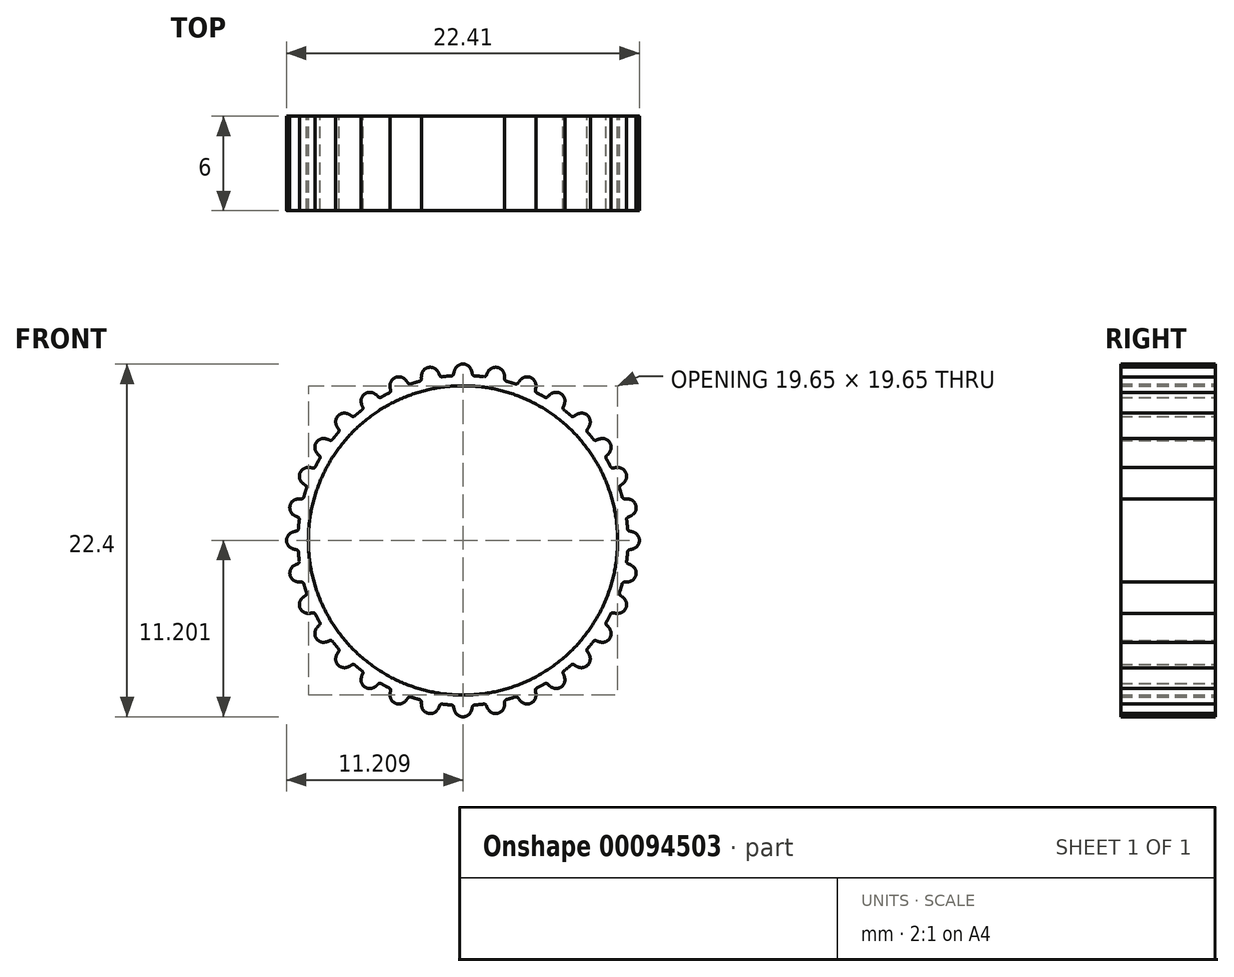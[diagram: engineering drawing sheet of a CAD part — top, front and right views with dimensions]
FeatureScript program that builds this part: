
annotation { "Feature Type Name" : "Feature", "Feature Type Description" : "" }
export const myFeature = defineFeature(function(context is Context, id is Id, definition is map)
    precondition{}
    {
        {
            var Q0;
            Q0=qCreatedBy(makeId("Front.planeOp"),FACE);
            var sketch = newSketch(context, id + "F0", { "sketchPlane" : qUnion([Q0])});
            skLineSegment(sketch, "E0", {"start": v(2.95, 2.18) * mm, "end": v(2.95, 0.8) * mm, "construction": true});
            skArc(sketch, "E1", {"start": v(2.95, 2.18) * mm, "mid": v(3.24, 2.1) * mm, "end": v(3.45, 1.87) * mm});
            skArc(sketch, "E2", {"start": v(3.45, 1.87) * mm, "mid": v(3.5, 1.72) * mm, "end": v(3.54, 1.56) * mm});
            skArc(sketch, "E3", {"start": v(3.54, 1.56) * mm, "mid": v(3.59, 1.48) * mm, "end": v(3.68, 1.43) * mm});
            skPoint(sketch, "E4", {"position": v(2.95, 0.8) * mm});
            skPoint(sketch, "E5", {"position": v(2.95, 1.43) * mm});
            skPoint(sketch, "E6", {"position": v(2.95, 1.18) * mm});
            skArc(sketch, "E7", {"start": v(2.95, 1.18) * mm, "mid": v(3.45, 1.17) * mm, "end": v(3.95, 1.13) * mm, "construction": true});
            skLineSegment(sketch, "E8", {"start": v(3.91, 0.76) * mm, "end": v(3.98, 1.4) * mm});
            skArc(sketch, "E9", {"start": v(3.68, 1.43) * mm, "mid": v(3.83, 1.42) * mm, "end": v(3.98, 1.4) * mm});
            skArc(sketch, "E10", {"start": v(2.95, 0.8) * mm, "mid": v(3.43, 0.8) * mm, "end": v(3.91, 0.76) * mm});
            skArc(sketch, "E11.MirrorCS", {"start": v(2.95, 2.18) * mm, "mid": v(2.65, 2.1) * mm, "end": v(2.45, 1.87) * mm});
            skArc(sketch, "E12.MirrorCS", {"start": v(2.45, 1.87) * mm, "mid": v(2.4, 1.72) * mm, "end": v(2.36, 1.56) * mm});
            skArc(sketch, "E13.MirrorCS", {"start": v(2.36, 1.56) * mm, "mid": v(2.31, 1.48) * mm, "end": v(2.22, 1.43) * mm});
            skArc(sketch, "E14.MirrorCS", {"start": v(2.22, 1.43) * mm, "mid": v(2.07, 1.42) * mm, "end": v(1.92, 1.4) * mm});
            skLineSegment(sketch, "E15.MirrorCS", {"start": v(1.99, 0.76) * mm, "end": v(1.92, 1.4) * mm});
            skArc(sketch, "E16.MirrorCS", {"start": v(2.95, 0.8) * mm, "mid": v(2.47, 0.8) * mm, "end": v(1.99, 0.76) * mm});
            skArc(sketch, "E17.1.0", {"start": v(0.33, 1.57) * mm, "mid": v(0.3, 1.4) * mm, "end": v(0.3, 1.25) * mm});
            skArc(sketch, "E17.1.1", {"start": v(0.76, 1.97) * mm, "mid": v(0.5, 1.83) * mm, "end": v(0.33, 1.57) * mm});
            skArc(sketch, "E17.1.2", {"start": v(1.03, 0.62) * mm, "mid": v(1.5, 0.7) * mm, "end": v(1.99, 0.76) * mm});
            skPoint(sketch, "E17.1.3", {"position": v(0.9, 1.23) * mm});
            skArc(sketch, "E17.1.4", {"start": v(1.31, 1.76) * mm, "mid": v(1.4, 1.62) * mm, "end": v(1.46, 1.48) * mm});
            skLineSegment(sketch, "E17.1.5", {"start": v(0.1, 0.38) * mm, "end": v(-0.1, 1) * mm});
            skArc(sketch, "E17.1.6", {"start": v(1.63, 1.38) * mm, "mid": v(1.77, 1.4) * mm, "end": v(1.92, 1.4) * mm});
            skArc(sketch, "E17.1.8", {"start": v(0.76, 1.97) * mm, "mid": v(1.07, 1.94) * mm, "end": v(1.31, 1.76) * mm});
            skPoint(sketch, "E17.1.9", {"position": v(1.03, 0.62) * mm});
            skArc(sketch, "E17.1.10", {"start": v(0.96, 0.98) * mm, "mid": v(1.45, 1.07) * mm, "end": v(1.95, 1.13) * mm, "construction": true});
            skArc(sketch, "E17.1.11", {"start": v(1.03, 0.62) * mm, "mid": v(0.56, 0.51) * mm, "end": v(0.1, 0.38) * mm});
            skPoint(sketch, "E17.1.12", {"position": v(0.96, 0.98) * mm});
            skArc(sketch, "E17.1.13", {"start": v(0.2, 1.1) * mm, "mid": v(0.05, 1.05) * mm, "end": v(-0.1, 1) * mm});
            skArc(sketch, "E17.1.14", {"start": v(1.46, 1.48) * mm, "mid": v(1.53, 1.4) * mm, "end": v(1.63, 1.38) * mm});
            skArc(sketch, "E17.1.15", {"start": v(0.3, 1.25) * mm, "mid": v(0.28, 1.15) * mm, "end": v(0.2, 1.1) * mm});
            skArc(sketch, "E17.2.0", {"start": v(-1.68, 0.85) * mm, "mid": v(-1.68, 0.7) * mm, "end": v(-1.65, 0.53) * mm});
            skArc(sketch, "E17.2.1", {"start": v(-1.34, 1.33) * mm, "mid": v(-1.58, 1.14) * mm, "end": v(-1.68, 0.85) * mm});
            skArc(sketch, "E17.2.2", {"start": v(-0.81, 0.06) * mm, "mid": v(-0.36, 0.23) * mm, "end": v(0.1, 0.38) * mm});
            skPoint(sketch, "E17.2.3", {"position": v(-1.05, 0.64) * mm});
            skArc(sketch, "E17.2.4", {"start": v(-0.76, 1.23) * mm, "mid": v(-0.65, 1.12) * mm, "end": v(-0.56, 0.99) * mm});
            skLineSegment(sketch, "E17.2.5", {"start": v(-1.68, -0.36) * mm, "end": v(-2, 0.22) * mm});
            skArc(sketch, "E17.2.6", {"start": v(-0.38, 0.92) * mm, "mid": v(-0.24, 0.96) * mm, "end": v(-0.1, 1) * mm});
            skLineSegment(sketch, "E17.2.7", {"start": v(0.1, 0.38) * mm, "end": v(-0.1, 1) * mm});
            skArc(sketch, "E17.2.8", {"start": v(-1.34, 1.33) * mm, "mid": v(-1.03, 1.37) * mm, "end": v(-0.76, 1.23) * mm});
            skPoint(sketch, "E17.2.9", {"position": v(-0.81, 0.06) * mm});
            skArc(sketch, "E17.2.10", {"start": v(-0.95, 0.4) * mm, "mid": v(-0.49, 0.58) * mm, "end": v(-0.01, 0.74) * mm, "construction": true});
            skArc(sketch, "E17.2.11", {"start": v(-0.81, 0.06) * mm, "mid": v(-1.25, -0.14) * mm, "end": v(-1.68, -0.36) * mm});
            skPoint(sketch, "E17.2.12", {"position": v(-0.95, 0.4) * mm});
            skArc(sketch, "E17.2.13", {"start": v(-1.73, 0.36) * mm, "mid": v(-1.86, 0.3) * mm, "end": v(-2, 0.22) * mm});
            skArc(sketch, "E17.2.14", {"start": v(-0.56, 0.99) * mm, "mid": v(-0.48, 0.92) * mm, "end": v(-0.38, 0.92) * mm});
            skArc(sketch, "E17.2.15", {"start": v(-1.65, 0.53) * mm, "mid": v(-1.66, 0.43) * mm, "end": v(-1.73, 0.36) * mm});
            skArc(sketch, "E17.3.0", {"start": v(-3.52, -0.24) * mm, "mid": v(-3.48, -0.4) * mm, "end": v(-3.42, -0.55) * mm});
            skArc(sketch, "E17.3.1", {"start": v(-3.28, 0.3) * mm, "mid": v(-3.47, 0.06) * mm, "end": v(-3.52, -0.24) * mm});
            skArc(sketch, "E17.3.2", {"start": v(-2.5, -0.85) * mm, "mid": v(-2.1, -0.6) * mm, "end": v(-1.68, -0.36) * mm});
            skPoint(sketch, "E17.3.3", {"position": v(-2.86, -0.33) * mm});
            skArc(sketch, "E17.3.4", {"start": v(-2.69, 0.31) * mm, "mid": v(-2.56, 0.22) * mm, "end": v(-2.44, 0.1) * mm});
            skLineSegment(sketch, "E17.3.5", {"start": v(-3.28, -1.43) * mm, "end": v(-3.7, -0.92) * mm});
            skArc(sketch, "E17.3.6", {"start": v(-2.25, 0.08) * mm, "mid": v(-2.12, 0.15) * mm, "end": v(-2, 0.22) * mm});
            skLineSegment(sketch, "E17.3.7", {"start": v(-1.68, -0.36) * mm, "end": v(-2, 0.22) * mm});
            skArc(sketch, "E17.3.8", {"start": v(-3.28, 0.3) * mm, "mid": v(-2.98, 0.39) * mm, "end": v(-2.69, 0.31) * mm});
            skPoint(sketch, "E17.3.9", {"position": v(-2.5, -0.85) * mm});
            skArc(sketch, "E17.3.10", {"start": v(-2.72, -0.54) * mm, "mid": v(-2.3, -0.27) * mm, "end": v(-1.86, -0.02) * mm, "construction": true});
            skArc(sketch, "E17.3.11", {"start": v(-2.5, -0.85) * mm, "mid": v(-2.9, -1.13) * mm, "end": v(-3.28, -1.43) * mm});
            skPoint(sketch, "E17.3.12", {"position": v(-2.72, -0.54) * mm});
            skArc(sketch, "E17.3.13", {"start": v(-3.47, -0.73) * mm, "mid": v(-3.58, -0.82) * mm, "end": v(-3.7, -0.92) * mm});
            skArc(sketch, "E17.3.14", {"start": v(-2.44, 0.1) * mm, "mid": v(-2.35, 0.06) * mm, "end": v(-2.25, 0.08) * mm});
            skArc(sketch, "E17.3.15", {"start": v(-3.42, -0.55) * mm, "mid": v(-3.41, -0.65) * mm, "end": v(-3.47, -0.73) * mm});
            skArc(sketch, "E17.4.0", {"start": v(-5.1, -1.67) * mm, "mid": v(-5.04, -1.82) * mm, "end": v(-4.95, -1.95) * mm});
            skArc(sketch, "E17.4.1", {"start": v(-4.97, -1.1) * mm, "mid": v(-5.12, -1.36) * mm, "end": v(-5.1, -1.67) * mm});
            skArc(sketch, "E17.4.2", {"start": v(-4, -2.07) * mm, "mid": v(-3.65, -1.74) * mm, "end": v(-3.28, -1.43) * mm});
            skPoint(sketch, "E17.4.3", {"position": v(-4.44, -1.63) * mm});
            skArc(sketch, "E17.4.4", {"start": v(-4.4, -0.96) * mm, "mid": v(-4.25, -1.03) * mm, "end": v(-4.12, -1.12) * mm});
            skLineSegment(sketch, "E17.4.5", {"start": v(-4.65, -2.79) * mm, "end": v(-5.15, -2.37) * mm});
            skArc(sketch, "E17.4.6", {"start": v(-3.93, -1.11) * mm, "mid": v(-3.81, -1.01) * mm, "end": v(-3.7, -0.92) * mm});
            skLineSegment(sketch, "E17.4.7", {"start": v(-3.28, -1.43) * mm, "end": v(-3.7, -0.92) * mm});
            skArc(sketch, "E17.4.8", {"start": v(-4.97, -1.1) * mm, "mid": v(-4.7, -0.95) * mm, "end": v(-4.4, -0.96) * mm});
            skPoint(sketch, "E17.4.9", {"position": v(-4, -2.07) * mm});
            skArc(sketch, "E17.4.10", {"start": v(-4.26, -1.8) * mm, "mid": v(-3.9, -1.46) * mm, "end": v(-3.52, -1.13) * mm, "construction": true});
            skArc(sketch, "E17.4.11", {"start": v(-4, -2.07) * mm, "mid": v(-4.33, -2.42) * mm, "end": v(-4.65, -2.79) * mm});
            skPoint(sketch, "E17.4.12", {"position": v(-4.26, -1.8) * mm});
            skArc(sketch, "E17.4.13", {"start": v(-4.96, -2.14) * mm, "mid": v(-5.06, -2.26) * mm, "end": v(-5.15, -2.37) * mm});
            skArc(sketch, "E17.4.14", {"start": v(-4.12, -1.12) * mm, "mid": v(-4.02, -1.15) * mm, "end": v(-3.93, -1.11) * mm});
            skArc(sketch, "E17.4.15", {"start": v(-4.95, -1.95) * mm, "mid": v(-4.92, -2.05) * mm, "end": v(-4.96, -2.14) * mm});
            skArc(sketch, "E17.5.0", {"start": v(-6.38, -3.38) * mm, "mid": v(-6.3, -3.52) * mm, "end": v(-6.18, -3.63) * mm});
            skArc(sketch, "E17.5.1", {"start": v(-6.37, -2.8) * mm, "mid": v(-6.46, -3.09) * mm, "end": v(-6.38, -3.38) * mm});
            skArc(sketch, "E17.5.2", {"start": v(-5.22, -3.56) * mm, "mid": v(-4.94, -3.17) * mm, "end": v(-4.65, -2.79) * mm});
            skPoint(sketch, "E17.5.3", {"position": v(-5.74, -3.21) * mm});
            skArc(sketch, "E17.5.4", {"start": v(-5.83, -2.55) * mm, "mid": v(-5.67, -2.59) * mm, "end": v(-5.52, -2.65) * mm});
            skLineSegment(sketch, "E17.5.5", {"start": v(-5.72, -4.39) * mm, "end": v(-6.3, -4.08) * mm});
            skArc(sketch, "E17.5.6", {"start": v(-5.34, -2.6) * mm, "mid": v(-5.25, -2.49) * mm, "end": v(-5.15, -2.37) * mm});
            skLineSegment(sketch, "E17.5.7", {"start": v(-4.65, -2.79) * mm, "end": v(-5.15, -2.37) * mm});
            skArc(sketch, "E17.5.8", {"start": v(-6.37, -2.8) * mm, "mid": v(-6.13, -2.6) * mm, "end": v(-5.83, -2.55) * mm});
            skPoint(sketch, "E17.5.9", {"position": v(-5.22, -3.56) * mm});
            skArc(sketch, "E17.5.10", {"start": v(-5.53, -3.35) * mm, "mid": v(-5.24, -2.94) * mm, "end": v(-4.94, -2.55) * mm, "construction": true});
            skArc(sketch, "E17.5.11", {"start": v(-5.22, -3.56) * mm, "mid": v(-5.48, -3.97) * mm, "end": v(-5.72, -4.39) * mm});
            skPoint(sketch, "E17.5.12", {"position": v(-5.53, -3.35) * mm});
            skArc(sketch, "E17.5.13", {"start": v(-6.15, -3.82) * mm, "mid": v(-6.22, -3.95) * mm, "end": v(-6.3, -4.08) * mm});
            skArc(sketch, "E17.5.14", {"start": v(-5.52, -2.65) * mm, "mid": v(-5.42, -2.66) * mm, "end": v(-5.34, -2.6) * mm});
            skArc(sketch, "E17.5.15", {"start": v(-6.18, -3.63) * mm, "mid": v(-6.13, -3.72) * mm, "end": v(-6.15, -3.82) * mm});
            skArc(sketch, "E17.6.0", {"start": v(-7.3, -5.31) * mm, "mid": v(-7.19, -5.42) * mm, "end": v(-7.06, -5.52) * mm});
            skArc(sketch, "E17.6.1", {"start": v(-7.4, -4.73) * mm, "mid": v(-7.44, -5.04) * mm, "end": v(-7.3, -5.31) * mm});
            skArc(sketch, "E17.6.2", {"start": v(-6.13, -5.26) * mm, "mid": v(-5.93, -4.82) * mm, "end": v(-5.71, -4.39) * mm});
            skPoint(sketch, "E17.6.3", {"position": v(-6.7, -5.02) * mm});
            skArc(sketch, "E17.6.4", {"start": v(-6.92, -4.4) * mm, "mid": v(-6.76, -4.4) * mm, "end": v(-6.6, -4.42) * mm});
            skLineSegment(sketch, "E17.6.5", {"start": v(-6.45, -6.17) * mm, "end": v(-7.08, -5.98) * mm});
            skArc(sketch, "E17.6.6", {"start": v(-6.43, -4.34) * mm, "mid": v(-6.36, -4.21) * mm, "end": v(-6.3, -4.08) * mm});
            skLineSegment(sketch, "E17.6.7", {"start": v(-5.71, -4.39) * mm, "end": v(-6.3, -4.08) * mm});
            skArc(sketch, "E17.6.8", {"start": v(-7.4, -4.73) * mm, "mid": v(-7.21, -4.5) * mm, "end": v(-6.92, -4.4) * mm});
            skPoint(sketch, "E17.6.9", {"position": v(-6.13, -5.26) * mm});
            skArc(sketch, "E17.6.10", {"start": v(-6.47, -5.12) * mm, "mid": v(-6.27, -4.66) * mm, "end": v(-6.05, -4.21) * mm, "construction": true});
            skArc(sketch, "E17.6.11", {"start": v(-6.13, -5.26) * mm, "mid": v(-6.3, -5.7) * mm, "end": v(-6.45, -6.17) * mm});
            skPoint(sketch, "E17.6.12", {"position": v(-6.47, -5.12) * mm});
            skArc(sketch, "E17.6.13", {"start": v(-6.99, -5.7) * mm, "mid": v(-7.04, -5.83) * mm, "end": v(-7.08, -5.98) * mm});
            skArc(sketch, "E17.6.14", {"start": v(-6.6, -4.42) * mm, "mid": v(-6.5, -4.41) * mm, "end": v(-6.43, -4.34) * mm});
            skArc(sketch, "E17.6.15", {"start": v(-7.06, -5.52) * mm, "mid": v(-7, -5.6) * mm, "end": v(-6.99, -5.7) * mm});
            skArc(sketch, "E17.7.0", {"start": v(-7.83, -7.38) * mm, "mid": v(-7.7, -7.47) * mm, "end": v(-7.55, -7.53) * mm});
            skArc(sketch, "E17.7.1", {"start": v(-8.04, -6.83) * mm, "mid": v(-8.01, -7.14) * mm, "end": v(-7.83, -7.38) * mm});
            skArc(sketch, "E17.7.2", {"start": v(-6.69, -7.1) * mm, "mid": v(-6.58, -6.63) * mm, "end": v(-6.45, -6.17) * mm});
            skPoint(sketch, "E17.7.3", {"position": v(-7.3, -6.98) * mm});
            skArc(sketch, "E17.7.4", {"start": v(-7.64, -6.4) * mm, "mid": v(-7.48, -6.38) * mm, "end": v(-7.32, -6.37) * mm});
            skLineSegment(sketch, "E17.7.5", {"start": v(-6.83, -8.06) * mm, "end": v(-7.48, -8) * mm});
            skArc(sketch, "E17.7.6", {"start": v(-7.16, -6.26) * mm, "mid": v(-7.12, -6.12) * mm, "end": v(-7.08, -5.98) * mm});
            skLineSegment(sketch, "E17.7.7", {"start": v(-6.45, -6.17) * mm, "end": v(-7.08, -5.98) * mm});
            skArc(sketch, "E17.7.8", {"start": v(-8.04, -6.83) * mm, "mid": v(-7.9, -6.56) * mm, "end": v(-7.64, -6.4) * mm});
            skPoint(sketch, "E17.7.9", {"position": v(-6.69, -7.1) * mm});
            skArc(sketch, "E17.7.10", {"start": v(-7.06, -7.03) * mm, "mid": v(-6.95, -6.54) * mm, "end": v(-6.81, -6.06) * mm, "construction": true});
            skArc(sketch, "E17.7.11", {"start": v(-6.69, -7.1) * mm, "mid": v(-6.77, -7.58) * mm, "end": v(-6.83, -8.06) * mm});
            skPoint(sketch, "E17.7.12", {"position": v(-7.06, -7.03) * mm});
            skArc(sketch, "E17.7.13", {"start": v(-7.45, -7.7) * mm, "mid": v(-7.46, -7.84) * mm, "end": v(-7.48, -8) * mm});
            skArc(sketch, "E17.7.14", {"start": v(-7.32, -6.37) * mm, "mid": v(-7.22, -6.35) * mm, "end": v(-7.16, -6.26) * mm});
            skArc(sketch, "E17.7.15", {"start": v(-7.55, -7.53) * mm, "mid": v(-7.47, -7.6) * mm, "end": v(-7.45, -7.7) * mm});
            skArc(sketch, "E17.8.0", {"start": v(-7.94, -9.52) * mm, "mid": v(-7.8, -9.58) * mm, "end": v(-7.64, -9.61) * mm});
            skArc(sketch, "E17.8.1", {"start": v(-8.26, -9.02) * mm, "mid": v(-8.17, -9.31) * mm, "end": v(-7.94, -9.52) * mm});
            skArc(sketch, "E17.8.2", {"start": v(-6.88, -9.02) * mm, "mid": v(-6.86, -8.54) * mm, "end": v(-6.83, -8.06) * mm});
            skPoint(sketch, "E17.8.3", {"position": v(-7.5, -9.02) * mm});
            skArc(sketch, "E17.8.4", {"start": v(-7.94, -8.52) * mm, "mid": v(-7.8, -8.46) * mm, "end": v(-7.64, -8.43) * mm});
            skLineSegment(sketch, "E17.8.5", {"start": v(-6.83, -9.98) * mm, "end": v(-7.48, -10.05) * mm});
            skArc(sketch, "E17.8.6", {"start": v(-7.5, -8.29) * mm, "mid": v(-7.5, -8.14) * mm, "end": v(-7.48, -8) * mm});
            skLineSegment(sketch, "E17.8.7", {"start": v(-6.83, -8.06) * mm, "end": v(-7.48, -8) * mm});
            skArc(sketch, "E17.8.8", {"start": v(-8.26, -9.02) * mm, "mid": v(-8.17, -8.73) * mm, "end": v(-7.94, -8.52) * mm});
            skPoint(sketch, "E17.8.9", {"position": v(-6.88, -9.02) * mm});
            skArc(sketch, "E17.8.10", {"start": v(-7.25, -9.02) * mm, "mid": v(-7.24, -8.52) * mm, "end": v(-7.2, -8.02) * mm, "construction": true});
            skArc(sketch, "E17.8.11", {"start": v(-6.88, -9.02) * mm, "mid": v(-6.86, -9.5) * mm, "end": v(-6.83, -9.98) * mm});
            skPoint(sketch, "E17.8.12", {"position": v(-7.25, -9.02) * mm});
            skArc(sketch, "E17.8.13", {"start": v(-7.5, -9.75) * mm, "mid": v(-7.5, -9.9) * mm, "end": v(-7.48, -10.05) * mm});
            skArc(sketch, "E17.8.14", {"start": v(-7.64, -8.43) * mm, "mid": v(-7.55, -8.38) * mm, "end": v(-7.5, -8.29) * mm});
            skArc(sketch, "E17.8.15", {"start": v(-7.64, -9.61) * mm, "mid": v(-7.55, -9.66) * mm, "end": v(-7.5, -9.75) * mm});
            skArc(sketch, "E17.9.0", {"start": v(-7.64, -11.63) * mm, "mid": v(-7.48, -11.66) * mm, "end": v(-7.32, -11.66) * mm});
            skArc(sketch, "E17.9.1", {"start": v(-8.04, -11.2) * mm, "mid": v(-7.9, -11.48) * mm, "end": v(-7.64, -11.63) * mm});
            skArc(sketch, "E17.9.2", {"start": v(-6.69, -10.94) * mm, "mid": v(-6.77, -10.46) * mm, "end": v(-6.83, -9.98) * mm});
            skPoint(sketch, "E17.9.3", {"position": v(-7.3, -11.06) * mm});
            skArc(sketch, "E17.9.4", {"start": v(-7.83, -10.66) * mm, "mid": v(-7.7, -10.57) * mm, "end": v(-7.55, -10.5) * mm});
            skLineSegment(sketch, "E17.9.5", {"start": v(-6.45, -11.87) * mm, "end": v(-7.08, -12.06) * mm});
            skArc(sketch, "E17.9.6", {"start": v(-7.45, -10.34) * mm, "mid": v(-7.46, -10.2) * mm, "end": v(-7.48, -10.05) * mm});
            skLineSegment(sketch, "E17.9.7", {"start": v(-6.83, -9.98) * mm, "end": v(-7.48, -10.05) * mm});
            skArc(sketch, "E17.9.8", {"start": v(-8.04, -11.2) * mm, "mid": v(-8.01, -10.9) * mm, "end": v(-7.83, -10.66) * mm});
            skPoint(sketch, "E17.9.9", {"position": v(-6.69, -10.94) * mm});
            skArc(sketch, "E17.9.10", {"start": v(-7.06, -11) * mm, "mid": v(-7.14, -10.52) * mm, "end": v(-7.2, -10.02) * mm, "construction": true});
            skArc(sketch, "E17.9.11", {"start": v(-6.69, -10.94) * mm, "mid": v(-6.58, -11.4) * mm, "end": v(-6.45, -11.87) * mm});
            skPoint(sketch, "E17.9.12", {"position": v(-7.06, -11) * mm});
            skArc(sketch, "E17.9.13", {"start": v(-7.16, -11.77) * mm, "mid": v(-7.12, -11.92) * mm, "end": v(-7.08, -12.06) * mm});
            skArc(sketch, "E17.9.14", {"start": v(-7.55, -10.5) * mm, "mid": v(-7.47, -10.44) * mm, "end": v(-7.45, -10.34) * mm});
            skArc(sketch, "E17.9.15", {"start": v(-7.32, -11.66) * mm, "mid": v(-7.22, -11.7) * mm, "end": v(-7.16, -11.77) * mm});
            skArc(sketch, "E17.10.0", {"start": v(-6.92, -13.65) * mm, "mid": v(-6.76, -13.65) * mm, "end": v(-6.6, -13.62) * mm});
            skArc(sketch, "E17.10.1", {"start": v(-7.4, -13.3) * mm, "mid": v(-7.21, -13.55) * mm, "end": v(-6.92, -13.65) * mm});
            skArc(sketch, "E17.10.2", {"start": v(-6.13, -12.78) * mm, "mid": v(-6.3, -12.33) * mm, "end": v(-6.45, -11.87) * mm});
            skPoint(sketch, "E17.10.3", {"position": v(-6.7, -13.02) * mm});
            skArc(sketch, "E17.10.4", {"start": v(-7.3, -12.73) * mm, "mid": v(-7.19, -12.61) * mm, "end": v(-7.06, -12.52) * mm});
            skLineSegment(sketch, "E17.10.5", {"start": v(-5.71, -13.65) * mm, "end": v(-6.3, -13.96) * mm});
            skArc(sketch, "E17.10.6", {"start": v(-6.99, -12.35) * mm, "mid": v(-7.04, -12.2) * mm, "end": v(-7.08, -12.06) * mm});
            skLineSegment(sketch, "E17.10.7", {"start": v(-6.45, -11.87) * mm, "end": v(-7.08, -12.06) * mm});
            skArc(sketch, "E17.10.8", {"start": v(-7.4, -13.3) * mm, "mid": v(-7.44, -13) * mm, "end": v(-7.3, -12.73) * mm});
            skPoint(sketch, "E17.10.9", {"position": v(-6.13, -12.78) * mm});
            skArc(sketch, "E17.10.10", {"start": v(-6.47, -12.92) * mm, "mid": v(-6.65, -12.46) * mm, "end": v(-6.81, -11.98) * mm, "construction": true});
            skArc(sketch, "E17.10.11", {"start": v(-6.13, -12.78) * mm, "mid": v(-5.93, -13.22) * mm, "end": v(-5.71, -13.65) * mm});
            skPoint(sketch, "E17.10.12", {"position": v(-6.47, -12.92) * mm});
            skArc(sketch, "E17.10.13", {"start": v(-6.43, -13.7) * mm, "mid": v(-6.36, -13.83) * mm, "end": v(-6.3, -13.96) * mm});
            skArc(sketch, "E17.10.14", {"start": v(-7.06, -12.52) * mm, "mid": v(-7, -12.45) * mm, "end": v(-6.99, -12.35) * mm});
            skArc(sketch, "E17.10.15", {"start": v(-6.6, -13.62) * mm, "mid": v(-6.5, -13.62) * mm, "end": v(-6.43, -13.7) * mm});
            skArc(sketch, "E17.11.0", {"start": v(-5.83, -15.49) * mm, "mid": v(-5.67, -15.45) * mm, "end": v(-5.52, -15.4) * mm});
            skArc(sketch, "E17.11.1", {"start": v(-6.37, -15.24) * mm, "mid": v(-6.13, -15.44) * mm, "end": v(-5.83, -15.49) * mm});
            skArc(sketch, "E17.11.2", {"start": v(-5.22, -14.48) * mm, "mid": v(-5.48, -14.07) * mm, "end": v(-5.72, -13.65) * mm});
            skPoint(sketch, "E17.11.3", {"position": v(-5.74, -14.83) * mm});
            skArc(sketch, "E17.11.4", {"start": v(-6.38, -14.66) * mm, "mid": v(-6.3, -14.52) * mm, "end": v(-6.18, -14.4) * mm});
            skLineSegment(sketch, "E17.11.5", {"start": v(-4.65, -15.25) * mm, "end": v(-5.15, -15.67) * mm});
            skArc(sketch, "E17.11.6", {"start": v(-6.15, -14.22) * mm, "mid": v(-6.22, -14.1) * mm, "end": v(-6.3, -13.96) * mm});
            skLineSegment(sketch, "E17.11.7", {"start": v(-5.72, -13.65) * mm, "end": v(-6.3, -13.96) * mm});
            skArc(sketch, "E17.11.8", {"start": v(-6.37, -15.24) * mm, "mid": v(-6.46, -14.95) * mm, "end": v(-6.38, -14.66) * mm});
            skPoint(sketch, "E17.11.9", {"position": v(-5.22, -14.48) * mm});
            skArc(sketch, "E17.11.10", {"start": v(-5.53, -14.69) * mm, "mid": v(-5.8, -14.26) * mm, "end": v(-6.05, -13.83) * mm, "construction": true});
            skArc(sketch, "E17.11.11", {"start": v(-5.22, -14.48) * mm, "mid": v(-4.94, -14.87) * mm, "end": v(-4.65, -15.25) * mm});
            skPoint(sketch, "E17.11.12", {"position": v(-5.53, -14.69) * mm});
            skArc(sketch, "E17.11.13", {"start": v(-5.34, -15.43) * mm, "mid": v(-5.25, -15.55) * mm, "end": v(-5.15, -15.67) * mm});
            skArc(sketch, "E17.11.14", {"start": v(-6.18, -14.4) * mm, "mid": v(-6.13, -14.32) * mm, "end": v(-6.15, -14.22) * mm});
            skArc(sketch, "E17.11.15", {"start": v(-5.52, -15.4) * mm, "mid": v(-5.42, -15.38) * mm, "end": v(-5.34, -15.43) * mm});
            skArc(sketch, "E17.12.0", {"start": v(-4.4, -17.07) * mm, "mid": v(-4.25, -17) * mm, "end": v(-4.12, -16.92) * mm});
            skArc(sketch, "E17.12.1", {"start": v(-4.97, -16.94) * mm, "mid": v(-4.7, -17.1) * mm, "end": v(-4.4, -17.07) * mm});
            skArc(sketch, "E17.12.2", {"start": v(-4, -15.97) * mm, "mid": v(-4.33, -15.62) * mm, "end": v(-4.65, -15.25) * mm});
            skPoint(sketch, "E17.12.3", {"position": v(-4.44, -16.41) * mm});
            skArc(sketch, "E17.12.4", {"start": v(-5.1, -16.37) * mm, "mid": v(-5.04, -16.22) * mm, "end": v(-4.95, -16.09) * mm});
            skLineSegment(sketch, "E17.12.5", {"start": v(-3.28, -16.61) * mm, "end": v(-3.7, -17.12) * mm});
            skArc(sketch, "E17.12.6", {"start": v(-4.96, -15.9) * mm, "mid": v(-5.06, -15.78) * mm, "end": v(-5.15, -15.67) * mm});
            skLineSegment(sketch, "E17.12.7", {"start": v(-4.65, -15.25) * mm, "end": v(-5.15, -15.67) * mm});
            skArc(sketch, "E17.12.8", {"start": v(-4.97, -16.94) * mm, "mid": v(-5.12, -16.67) * mm, "end": v(-5.1, -16.37) * mm});
            skPoint(sketch, "E17.12.9", {"position": v(-4, -15.97) * mm});
            skArc(sketch, "E17.12.10", {"start": v(-4.26, -16.23) * mm, "mid": v(-4.6, -15.87) * mm, "end": v(-4.94, -15.5) * mm, "construction": true});
            skArc(sketch, "E17.12.11", {"start": v(-4, -15.97) * mm, "mid": v(-3.65, -16.3) * mm, "end": v(-3.28, -16.61) * mm});
            skPoint(sketch, "E17.12.12", {"position": v(-4.26, -16.23) * mm});
            skArc(sketch, "E17.12.13", {"start": v(-3.93, -16.93) * mm, "mid": v(-3.81, -17.02) * mm, "end": v(-3.7, -17.12) * mm});
            skArc(sketch, "E17.12.14", {"start": v(-4.95, -16.09) * mm, "mid": v(-4.92, -15.99) * mm, "end": v(-4.96, -15.9) * mm});
            skArc(sketch, "E17.12.15", {"start": v(-4.12, -16.92) * mm, "mid": v(-4.02, -16.9) * mm, "end": v(-3.93, -16.93) * mm});
            skArc(sketch, "E17.13.0", {"start": v(-2.69, -18.35) * mm, "mid": v(-2.56, -18.26) * mm, "end": v(-2.44, -18.15) * mm});
            skArc(sketch, "E17.13.1", {"start": v(-3.28, -18.34) * mm, "mid": v(-2.98, -18.43) * mm, "end": v(-2.69, -18.35) * mm});
            skArc(sketch, "E17.13.2", {"start": v(-2.5, -17.19) * mm, "mid": v(-2.9, -16.91) * mm, "end": v(-3.28, -16.61) * mm});
            skPoint(sketch, "E17.13.3", {"position": v(-2.86, -17.71) * mm});
            skArc(sketch, "E17.13.4", {"start": v(-3.52, -17.8) * mm, "mid": v(-3.48, -17.64) * mm, "end": v(-3.42, -17.5) * mm});
            skLineSegment(sketch, "E17.13.5", {"start": v(-1.68, -17.68) * mm, "end": v(-2, -18.26) * mm});
            skArc(sketch, "E17.13.6", {"start": v(-3.47, -17.3) * mm, "mid": v(-3.58, -17.21) * mm, "end": v(-3.7, -17.12) * mm});
            skLineSegment(sketch, "E17.13.7", {"start": v(-3.28, -16.61) * mm, "end": v(-3.7, -17.12) * mm});
            skArc(sketch, "E17.13.8", {"start": v(-3.28, -18.34) * mm, "mid": v(-3.47, -18.1) * mm, "end": v(-3.52, -17.8) * mm});
            skPoint(sketch, "E17.13.9", {"position": v(-2.5, -17.19) * mm});
            skArc(sketch, "E17.13.10", {"start": v(-2.72, -17.5) * mm, "mid": v(-3.13, -17.21) * mm, "end": v(-3.52, -16.9) * mm, "construction": true});
            skArc(sketch, "E17.13.11", {"start": v(-2.5, -17.19) * mm, "mid": v(-2.1, -17.45) * mm, "end": v(-1.68, -17.68) * mm});
            skPoint(sketch, "E17.13.12", {"position": v(-2.72, -17.5) * mm});
            skArc(sketch, "E17.13.13", {"start": v(-2.25, -18.12) * mm, "mid": v(-2.12, -18.2) * mm, "end": v(-2, -18.26) * mm});
            skArc(sketch, "E17.13.14", {"start": v(-3.42, -17.5) * mm, "mid": v(-3.41, -17.4) * mm, "end": v(-3.47, -17.3) * mm});
            skArc(sketch, "E17.13.15", {"start": v(-2.44, -18.15) * mm, "mid": v(-2.35, -18.1) * mm, "end": v(-2.25, -18.12) * mm});
            skArc(sketch, "E17.14.0", {"start": v(-0.76, -19.27) * mm, "mid": v(-0.65, -19.16) * mm, "end": v(-0.56, -19.02) * mm});
            skArc(sketch, "E17.14.1", {"start": v(-1.34, -19.37) * mm, "mid": v(-1.03, -19.4) * mm, "end": v(-0.76, -19.27) * mm});
            skArc(sketch, "E17.14.2", {"start": v(-0.81, -18.1) * mm, "mid": v(-1.25, -17.9) * mm, "end": v(-1.68, -17.68) * mm});
            skPoint(sketch, "E17.14.3", {"position": v(-1.05, -18.68) * mm});
            skArc(sketch, "E17.14.4", {"start": v(-1.68, -18.9) * mm, "mid": v(-1.68, -18.73) * mm, "end": v(-1.65, -18.57) * mm});
            skLineSegment(sketch, "E17.14.5", {"start": v(0.1, -18.42) * mm, "end": v(-0.1, -19.05) * mm});
            skArc(sketch, "E17.14.6", {"start": v(-1.73, -18.4) * mm, "mid": v(-1.86, -18.33) * mm, "end": v(-2, -18.26) * mm});
            skLineSegment(sketch, "E17.14.7", {"start": v(-1.68, -17.68) * mm, "end": v(-2, -18.26) * mm});
            skArc(sketch, "E17.14.8", {"start": v(-1.34, -19.37) * mm, "mid": v(-1.58, -19.18) * mm, "end": v(-1.68, -18.9) * mm});
            skPoint(sketch, "E17.14.9", {"position": v(-0.81, -18.1) * mm});
            skArc(sketch, "E17.14.10", {"start": v(-0.95, -18.44) * mm, "mid": v(-1.41, -18.24) * mm, "end": v(-1.86, -18.01) * mm, "construction": true});
            skArc(sketch, "E17.14.11", {"start": v(-0.81, -18.1) * mm, "mid": v(-0.36, -18.27) * mm, "end": v(0.1, -18.42) * mm});
            skPoint(sketch, "E17.14.12", {"position": v(-0.95, -18.44) * mm});
            skArc(sketch, "E17.14.13", {"start": v(-0.38, -18.96) * mm, "mid": v(-0.24, -19) * mm, "end": v(-0.1, -19.05) * mm});
            skArc(sketch, "E17.14.14", {"start": v(-1.65, -18.57) * mm, "mid": v(-1.66, -18.47) * mm, "end": v(-1.73, -18.4) * mm});
            skArc(sketch, "E17.14.15", {"start": v(-0.56, -19.02) * mm, "mid": v(-0.48, -18.96) * mm, "end": v(-0.38, -18.96) * mm});
            skArc(sketch, "E17.15.0", {"start": v(1.31, -19.8) * mm, "mid": v(1.4, -19.66) * mm, "end": v(1.46, -19.52) * mm});
            skArc(sketch, "E17.15.1", {"start": v(0.76, -20) * mm, "mid": v(1.07, -19.98) * mm, "end": v(1.31, -19.8) * mm});
            skArc(sketch, "E17.15.2", {"start": v(1.03, -18.65) * mm, "mid": v(0.56, -18.55) * mm, "end": v(0.1, -18.42) * mm});
            skPoint(sketch, "E17.15.3", {"position": v(0.9, -19.27) * mm});
            skArc(sketch, "E17.15.4", {"start": v(0.33, -19.6) * mm, "mid": v(0.3, -19.45) * mm, "end": v(0.3, -19.28) * mm});
            skLineSegment(sketch, "E17.15.5", {"start": v(1.99, -18.8) * mm, "end": v(1.92, -19.45) * mm});
            skArc(sketch, "E17.15.6", {"start": v(0.2, -19.13) * mm, "mid": v(0.05, -19.09) * mm, "end": v(-0.1, -19.05) * mm});
            skLineSegment(sketch, "E17.15.7", {"start": v(0.1, -18.42) * mm, "end": v(-0.1, -19.05) * mm});
            skArc(sketch, "E17.15.8", {"start": v(0.76, -20) * mm, "mid": v(0.5, -19.87) * mm, "end": v(0.33, -19.6) * mm});
            skPoint(sketch, "E17.15.9", {"position": v(1.03, -18.65) * mm});
            skArc(sketch, "E17.15.10", {"start": v(0.96, -19.02) * mm, "mid": v(0.47, -18.91) * mm, "end": v(-0.01, -18.78) * mm, "construction": true});
            skArc(sketch, "E17.15.11", {"start": v(1.03, -18.65) * mm, "mid": v(1.5, -18.74) * mm, "end": v(1.99, -18.8) * mm});
            skPoint(sketch, "E17.15.12", {"position": v(0.96, -19.02) * mm});
            skArc(sketch, "E17.15.13", {"start": v(1.63, -19.41) * mm, "mid": v(1.77, -19.43) * mm, "end": v(1.92, -19.45) * mm});
            skArc(sketch, "E17.15.14", {"start": v(0.3, -19.28) * mm, "mid": v(0.28, -19.19) * mm, "end": v(0.2, -19.13) * mm});
            skArc(sketch, "E17.15.15", {"start": v(1.46, -19.52) * mm, "mid": v(1.53, -19.44) * mm, "end": v(1.63, -19.41) * mm});
            skArc(sketch, "E17.16.0", {"start": v(3.45, -19.91) * mm, "mid": v(3.5, -19.76) * mm, "end": v(3.54, -19.6) * mm});
            skArc(sketch, "E17.16.1", {"start": v(2.95, -20.22) * mm, "mid": v(3.24, -20.14) * mm, "end": v(3.45, -19.91) * mm});
            skArc(sketch, "E17.16.2", {"start": v(2.95, -18.84) * mm, "mid": v(2.47, -18.83) * mm, "end": v(1.99, -18.8) * mm});
            skPoint(sketch, "E17.16.3", {"position": v(2.95, -19.47) * mm});
            skArc(sketch, "E17.16.4", {"start": v(2.45, -19.91) * mm, "mid": v(2.4, -19.76) * mm, "end": v(2.36, -19.6) * mm});
            skLineSegment(sketch, "E17.16.5", {"start": v(3.91, -18.8) * mm, "end": v(3.98, -19.45) * mm});
            skArc(sketch, "E17.16.6", {"start": v(2.22, -19.47) * mm, "mid": v(2.07, -19.46) * mm, "end": v(1.92, -19.45) * mm});
            skLineSegment(sketch, "E17.16.7", {"start": v(1.99, -18.8) * mm, "end": v(1.92, -19.45) * mm});
            skArc(sketch, "E17.16.8", {"start": v(2.95, -20.22) * mm, "mid": v(2.65, -20.14) * mm, "end": v(2.45, -19.91) * mm});
            skPoint(sketch, "E17.16.9", {"position": v(2.95, -18.84) * mm});
            skArc(sketch, "E17.16.10", {"start": v(2.95, -19.22) * mm, "mid": v(2.45, -19.2) * mm, "end": v(1.95, -19.17) * mm, "construction": true});
            skArc(sketch, "E17.16.11", {"start": v(2.95, -18.84) * mm, "mid": v(3.43, -18.83) * mm, "end": v(3.91, -18.8) * mm});
            skPoint(sketch, "E17.16.12", {"position": v(2.95, -19.22) * mm});
            skArc(sketch, "E17.16.13", {"start": v(3.68, -19.47) * mm, "mid": v(3.83, -19.46) * mm, "end": v(3.98, -19.45) * mm});
            skArc(sketch, "E17.16.14", {"start": v(2.36, -19.6) * mm, "mid": v(2.31, -19.51) * mm, "end": v(2.22, -19.47) * mm});
            skArc(sketch, "E17.16.15", {"start": v(3.54, -19.6) * mm, "mid": v(3.59, -19.51) * mm, "end": v(3.68, -19.47) * mm});
            skArc(sketch, "E17.17.0", {"start": v(5.56, -19.6) * mm, "mid": v(5.6, -19.45) * mm, "end": v(5.6, -19.28) * mm});
            skArc(sketch, "E17.17.1", {"start": v(5.13, -20) * mm, "mid": v(5.4, -19.87) * mm, "end": v(5.56, -19.6) * mm});
            skArc(sketch, "E17.17.2", {"start": v(4.87, -18.65) * mm, "mid": v(4.4, -18.74) * mm, "end": v(3.91, -18.8) * mm});
            skPoint(sketch, "E17.17.3", {"position": v(4.99, -19.27) * mm});
            skArc(sketch, "E17.17.4", {"start": v(4.58, -19.8) * mm, "mid": v(4.5, -19.66) * mm, "end": v(4.43, -19.52) * mm});
            skLineSegment(sketch, "E17.17.5", {"start": v(5.8, -18.42) * mm, "end": v(6, -19.05) * mm});
            skArc(sketch, "E17.17.6", {"start": v(4.27, -19.41) * mm, "mid": v(4.12, -19.43) * mm, "end": v(3.98, -19.45) * mm});
            skLineSegment(sketch, "E17.17.7", {"start": v(3.91, -18.8) * mm, "end": v(3.98, -19.45) * mm});
            skArc(sketch, "E17.17.8", {"start": v(5.13, -20) * mm, "mid": v(4.83, -19.98) * mm, "end": v(4.58, -19.8) * mm});
            skPoint(sketch, "E17.17.9", {"position": v(4.87, -18.65) * mm});
            skArc(sketch, "E17.17.10", {"start": v(4.94, -19.02) * mm, "mid": v(4.45, -19.1) * mm, "end": v(3.95, -19.17) * mm, "construction": true});
            skArc(sketch, "E17.17.11", {"start": v(4.87, -18.65) * mm, "mid": v(5.34, -18.55) * mm, "end": v(5.8, -18.42) * mm});
            skPoint(sketch, "E17.17.12", {"position": v(4.94, -19.02) * mm});
            skArc(sketch, "E17.17.13", {"start": v(5.7, -19.13) * mm, "mid": v(5.85, -19.09) * mm, "end": v(6, -19.05) * mm});
            skArc(sketch, "E17.17.14", {"start": v(4.43, -19.52) * mm, "mid": v(4.37, -19.44) * mm, "end": v(4.27, -19.41) * mm});
            skArc(sketch, "E17.17.15", {"start": v(5.6, -19.28) * mm, "mid": v(5.62, -19.19) * mm, "end": v(5.7, -19.13) * mm});
            skArc(sketch, "E17.18.0", {"start": v(7.58, -18.9) * mm, "mid": v(7.57, -18.73) * mm, "end": v(7.55, -18.57) * mm});
            skArc(sketch, "E17.18.1", {"start": v(7.24, -19.37) * mm, "mid": v(7.48, -19.18) * mm, "end": v(7.58, -18.9) * mm});
            skArc(sketch, "E17.18.2", {"start": v(6.7, -18.1) * mm, "mid": v(6.26, -18.27) * mm, "end": v(5.8, -18.42) * mm});
            skPoint(sketch, "E17.18.3", {"position": v(6.95, -18.68) * mm});
            skArc(sketch, "E17.18.4", {"start": v(6.66, -19.27) * mm, "mid": v(6.54, -19.16) * mm, "end": v(6.45, -19.02) * mm});
            skLineSegment(sketch, "E17.18.5", {"start": v(7.58, -17.68) * mm, "end": v(7.89, -18.26) * mm});
            skArc(sketch, "E17.18.6", {"start": v(6.28, -18.96) * mm, "mid": v(6.13, -19) * mm, "end": v(6, -19.05) * mm});
            skLineSegment(sketch, "E17.18.7", {"start": v(5.8, -18.42) * mm, "end": v(6, -19.05) * mm});
            skArc(sketch, "E17.18.8", {"start": v(7.24, -19.37) * mm, "mid": v(6.93, -19.4) * mm, "end": v(6.66, -19.27) * mm});
            skPoint(sketch, "E17.18.9", {"position": v(6.7, -18.1) * mm});
            skArc(sketch, "E17.18.10", {"start": v(6.85, -18.44) * mm, "mid": v(6.39, -18.62) * mm, "end": v(5.9, -18.78) * mm, "construction": true});
            skArc(sketch, "E17.18.11", {"start": v(6.7, -18.1) * mm, "mid": v(7.15, -17.9) * mm, "end": v(7.58, -17.68) * mm});
            skPoint(sketch, "E17.18.12", {"position": v(6.85, -18.44) * mm});
            skArc(sketch, "E17.18.13", {"start": v(7.62, -18.4) * mm, "mid": v(7.76, -18.33) * mm, "end": v(7.89, -18.26) * mm});
            skArc(sketch, "E17.18.14", {"start": v(6.45, -19.02) * mm, "mid": v(6.38, -18.96) * mm, "end": v(6.28, -18.96) * mm});
            skArc(sketch, "E17.18.15", {"start": v(7.55, -18.57) * mm, "mid": v(7.55, -18.47) * mm, "end": v(7.62, -18.4) * mm});
            skArc(sketch, "E17.19.0", {"start": v(9.42, -17.8) * mm, "mid": v(9.38, -17.64) * mm, "end": v(9.32, -17.5) * mm});
            skArc(sketch, "E17.19.1", {"start": v(9.17, -18.34) * mm, "mid": v(9.37, -18.1) * mm, "end": v(9.42, -17.8) * mm});
            skArc(sketch, "E17.19.2", {"start": v(8.4, -17.19) * mm, "mid": v(8, -17.45) * mm, "end": v(7.58, -17.68) * mm});
            skPoint(sketch, "E17.19.3", {"position": v(8.76, -17.71) * mm});
            skArc(sketch, "E17.19.4", {"start": v(8.59, -18.35) * mm, "mid": v(8.45, -18.26) * mm, "end": v(8.34, -18.15) * mm});
            skLineSegment(sketch, "E17.19.5", {"start": v(9.18, -16.61) * mm, "end": v(9.6, -17.12) * mm});
            skArc(sketch, "E17.19.6", {"start": v(8.15, -18.12) * mm, "mid": v(8.02, -18.2) * mm, "end": v(7.89, -18.26) * mm});
            skLineSegment(sketch, "E17.19.7", {"start": v(7.58, -17.68) * mm, "end": v(7.89, -18.26) * mm});
            skArc(sketch, "E17.19.8", {"start": v(9.17, -18.34) * mm, "mid": v(8.88, -18.43) * mm, "end": v(8.59, -18.35) * mm});
            skPoint(sketch, "E17.19.9", {"position": v(8.4, -17.19) * mm});
            skArc(sketch, "E17.19.10", {"start": v(8.62, -17.5) * mm, "mid": v(8.2, -17.77) * mm, "end": v(7.76, -18.02) * mm, "construction": true});
            skArc(sketch, "E17.19.11", {"start": v(8.4, -17.19) * mm, "mid": v(8.8, -16.91) * mm, "end": v(9.18, -16.61) * mm});
            skPoint(sketch, "E17.19.12", {"position": v(8.62, -17.5) * mm});
            skArc(sketch, "E17.19.13", {"start": v(9.36, -17.3) * mm, "mid": v(9.48, -17.21) * mm, "end": v(9.6, -17.12) * mm});
            skArc(sketch, "E17.19.14", {"start": v(8.34, -18.15) * mm, "mid": v(8.25, -18.1) * mm, "end": v(8.15, -18.12) * mm});
            skArc(sketch, "E17.19.15", {"start": v(9.32, -17.5) * mm, "mid": v(9.3, -17.4) * mm, "end": v(9.36, -17.3) * mm});
            skArc(sketch, "E17.20.0", {"start": v(11, -16.37) * mm, "mid": v(10.94, -16.22) * mm, "end": v(10.85, -16.09) * mm});
            skArc(sketch, "E17.20.1", {"start": v(10.87, -16.94) * mm, "mid": v(11.02, -16.67) * mm, "end": v(11, -16.37) * mm});
            skArc(sketch, "E17.20.2", {"start": v(9.9, -15.97) * mm, "mid": v(9.55, -16.3) * mm, "end": v(9.18, -16.61) * mm});
            skPoint(sketch, "E17.20.3", {"position": v(10.34, -16.41) * mm});
            skArc(sketch, "E17.20.4", {"start": v(10.3, -17.07) * mm, "mid": v(10.15, -17) * mm, "end": v(10.01, -16.92) * mm});
            skLineSegment(sketch, "E17.20.5", {"start": v(10.54, -15.25) * mm, "end": v(11.05, -15.67) * mm});
            skArc(sketch, "E17.20.6", {"start": v(9.82, -16.93) * mm, "mid": v(9.71, -17.02) * mm, "end": v(9.6, -17.12) * mm});
            skLineSegment(sketch, "E17.20.7", {"start": v(9.18, -16.61) * mm, "end": v(9.6, -17.12) * mm});
            skArc(sketch, "E17.20.8", {"start": v(10.87, -16.94) * mm, "mid": v(10.6, -17.1) * mm, "end": v(10.3, -17.07) * mm});
            skPoint(sketch, "E17.20.9", {"position": v(9.9, -15.97) * mm});
            skArc(sketch, "E17.20.10", {"start": v(10.16, -16.23) * mm, "mid": v(9.8, -16.58) * mm, "end": v(9.42, -16.9) * mm, "construction": true});
            skArc(sketch, "E17.20.11", {"start": v(9.9, -15.97) * mm, "mid": v(10.23, -15.62) * mm, "end": v(10.54, -15.25) * mm});
            skPoint(sketch, "E17.20.12", {"position": v(10.16, -16.23) * mm});
            skArc(sketch, "E17.20.13", {"start": v(10.86, -15.9) * mm, "mid": v(10.95, -15.78) * mm, "end": v(11.05, -15.67) * mm});
            skArc(sketch, "E17.20.14", {"start": v(10.01, -16.92) * mm, "mid": v(9.92, -16.9) * mm, "end": v(9.82, -16.93) * mm});
            skArc(sketch, "E17.20.15", {"start": v(10.85, -16.09) * mm, "mid": v(10.82, -15.99) * mm, "end": v(10.86, -15.9) * mm});
            skArc(sketch, "E17.21.0", {"start": v(12.28, -14.66) * mm, "mid": v(12.2, -14.52) * mm, "end": v(12.08, -14.4) * mm});
            skArc(sketch, "E17.21.1", {"start": v(12.26, -15.24) * mm, "mid": v(12.36, -14.95) * mm, "end": v(12.28, -14.66) * mm});
            skArc(sketch, "E17.21.2", {"start": v(11.12, -14.48) * mm, "mid": v(10.84, -14.87) * mm, "end": v(10.54, -15.25) * mm});
            skPoint(sketch, "E17.21.3", {"position": v(11.64, -14.83) * mm});
            skArc(sketch, "E17.21.4", {"start": v(11.73, -15.49) * mm, "mid": v(11.57, -15.45) * mm, "end": v(11.42, -15.4) * mm});
            skLineSegment(sketch, "E17.21.5", {"start": v(11.61, -13.65) * mm, "end": v(12.2, -13.96) * mm});
            skArc(sketch, "E17.21.6", {"start": v(11.24, -15.43) * mm, "mid": v(11.14, -15.55) * mm, "end": v(11.05, -15.67) * mm});
            skLineSegment(sketch, "E17.21.7", {"start": v(10.54, -15.25) * mm, "end": v(11.05, -15.67) * mm});
            skArc(sketch, "E17.21.8", {"start": v(12.26, -15.24) * mm, "mid": v(12.03, -15.44) * mm, "end": v(11.73, -15.49) * mm});
            skPoint(sketch, "E17.21.9", {"position": v(11.12, -14.48) * mm});
            skArc(sketch, "E17.21.10", {"start": v(11.43, -14.69) * mm, "mid": v(11.14, -15.1) * mm, "end": v(10.83, -15.5) * mm, "construction": true});
            skArc(sketch, "E17.21.11", {"start": v(11.12, -14.48) * mm, "mid": v(11.38, -14.07) * mm, "end": v(11.61, -13.65) * mm});
            skPoint(sketch, "E17.21.12", {"position": v(11.43, -14.69) * mm});
            skArc(sketch, "E17.21.13", {"start": v(12.05, -14.22) * mm, "mid": v(12.12, -14.1) * mm, "end": v(12.2, -13.96) * mm});
            skArc(sketch, "E17.21.14", {"start": v(11.42, -15.4) * mm, "mid": v(11.32, -15.38) * mm, "end": v(11.24, -15.43) * mm});
            skArc(sketch, "E17.21.15", {"start": v(12.08, -14.4) * mm, "mid": v(12.03, -14.32) * mm, "end": v(12.05, -14.22) * mm});
            skArc(sketch, "E17.22.0", {"start": v(13.2, -12.73) * mm, "mid": v(13.09, -12.61) * mm, "end": v(12.95, -12.52) * mm});
            skArc(sketch, "E17.22.1", {"start": v(13.3, -13.3) * mm, "mid": v(13.33, -13) * mm, "end": v(13.2, -12.73) * mm});
            skArc(sketch, "E17.22.2", {"start": v(12.03, -12.78) * mm, "mid": v(11.83, -13.22) * mm, "end": v(11.61, -13.65) * mm});
            skPoint(sketch, "E17.22.3", {"position": v(12.6, -13.02) * mm});
            skArc(sketch, "E17.22.4", {"start": v(12.82, -13.65) * mm, "mid": v(12.66, -13.65) * mm, "end": v(12.5, -13.62) * mm});
            skLineSegment(sketch, "E17.22.5", {"start": v(12.35, -11.87) * mm, "end": v(12.98, -12.06) * mm});
            skArc(sketch, "E17.22.6", {"start": v(12.33, -13.7) * mm, "mid": v(12.26, -13.83) * mm, "end": v(12.2, -13.96) * mm});
            skLineSegment(sketch, "E17.22.7", {"start": v(11.61, -13.65) * mm, "end": v(12.2, -13.96) * mm});
            skArc(sketch, "E17.22.8", {"start": v(13.3, -13.3) * mm, "mid": v(13.1, -13.55) * mm, "end": v(12.82, -13.65) * mm});
            skPoint(sketch, "E17.22.9", {"position": v(12.03, -12.78) * mm});
            skArc(sketch, "E17.22.10", {"start": v(12.37, -12.92) * mm, "mid": v(12.17, -13.38) * mm, "end": v(11.94, -13.83) * mm, "construction": true});
            skArc(sketch, "E17.22.11", {"start": v(12.03, -12.78) * mm, "mid": v(12.2, -12.33) * mm, "end": v(12.35, -11.87) * mm});
            skPoint(sketch, "E17.22.12", {"position": v(12.37, -12.92) * mm});
            skArc(sketch, "E17.22.13", {"start": v(12.89, -12.35) * mm, "mid": v(12.93, -12.2) * mm, "end": v(12.98, -12.06) * mm});
            skArc(sketch, "E17.22.14", {"start": v(12.5, -13.62) * mm, "mid": v(12.4, -13.62) * mm, "end": v(12.33, -13.7) * mm});
            skArc(sketch, "E17.22.15", {"start": v(12.95, -12.52) * mm, "mid": v(12.89, -12.45) * mm, "end": v(12.89, -12.35) * mm});
            skArc(sketch, "E17.23.0", {"start": v(13.73, -10.66) * mm, "mid": v(13.6, -10.57) * mm, "end": v(13.45, -10.5) * mm});
            skArc(sketch, "E17.23.1", {"start": v(13.94, -11.2) * mm, "mid": v(13.91, -10.9) * mm, "end": v(13.73, -10.66) * mm});
            skArc(sketch, "E17.23.2", {"start": v(12.58, -10.94) * mm, "mid": v(12.48, -11.4) * mm, "end": v(12.35, -11.87) * mm});
            skPoint(sketch, "E17.23.3", {"position": v(13.2, -11.06) * mm});
            skArc(sketch, "E17.23.4", {"start": v(13.53, -11.63) * mm, "mid": v(13.38, -11.66) * mm, "end": v(13.21, -11.66) * mm});
            skLineSegment(sketch, "E17.23.5", {"start": v(12.73, -9.98) * mm, "end": v(13.38, -10.05) * mm});
            skArc(sketch, "E17.23.6", {"start": v(13.06, -11.77) * mm, "mid": v(13.02, -11.92) * mm, "end": v(12.98, -12.06) * mm});
            skLineSegment(sketch, "E17.23.7", {"start": v(12.35, -11.87) * mm, "end": v(12.98, -12.06) * mm});
            skArc(sketch, "E17.23.8", {"start": v(13.94, -11.2) * mm, "mid": v(13.8, -11.48) * mm, "end": v(13.53, -11.63) * mm});
            skPoint(sketch, "E17.23.9", {"position": v(12.58, -10.94) * mm});
            skArc(sketch, "E17.23.10", {"start": v(12.95, -11) * mm, "mid": v(12.84, -11.5) * mm, "end": v(12.7, -11.98) * mm, "construction": true});
            skArc(sketch, "E17.23.11", {"start": v(12.58, -10.94) * mm, "mid": v(12.67, -10.46) * mm, "end": v(12.73, -9.98) * mm});
            skPoint(sketch, "E17.23.12", {"position": v(12.95, -11) * mm});
            skArc(sketch, "E17.23.13", {"start": v(13.34, -10.34) * mm, "mid": v(13.36, -10.2) * mm, "end": v(13.38, -10.05) * mm});
            skArc(sketch, "E17.23.14", {"start": v(13.21, -11.66) * mm, "mid": v(13.12, -11.7) * mm, "end": v(13.06, -11.77) * mm});
            skArc(sketch, "E17.23.15", {"start": v(13.45, -10.5) * mm, "mid": v(13.37, -10.44) * mm, "end": v(13.34, -10.34) * mm});
            skArc(sketch, "E17.24.0", {"start": v(13.84, -8.52) * mm, "mid": v(13.7, -8.46) * mm, "end": v(13.53, -8.43) * mm});
            skArc(sketch, "E17.24.1", {"start": v(14.15, -9.02) * mm, "mid": v(14.07, -8.73) * mm, "end": v(13.84, -8.52) * mm});
            skArc(sketch, "E17.24.2", {"start": v(12.77, -9.02) * mm, "mid": v(12.76, -9.5) * mm, "end": v(12.73, -9.98) * mm});
            skPoint(sketch, "E17.24.3", {"position": v(13.4, -9.02) * mm});
            skArc(sketch, "E17.24.4", {"start": v(13.84, -9.52) * mm, "mid": v(13.7, -9.58) * mm, "end": v(13.53, -9.61) * mm});
            skLineSegment(sketch, "E17.24.5", {"start": v(12.73, -8.06) * mm, "end": v(13.38, -8) * mm});
            skArc(sketch, "E17.24.6", {"start": v(13.4, -9.75) * mm, "mid": v(13.4, -9.9) * mm, "end": v(13.38, -10.05) * mm});
            skLineSegment(sketch, "E17.24.7", {"start": v(12.73, -9.98) * mm, "end": v(13.38, -10.05) * mm});
            skArc(sketch, "E17.24.8", {"start": v(14.15, -9.02) * mm, "mid": v(14.07, -9.31) * mm, "end": v(13.84, -9.52) * mm});
            skPoint(sketch, "E17.24.9", {"position": v(12.77, -9.02) * mm});
            skArc(sketch, "E17.24.10", {"start": v(13.15, -9.02) * mm, "mid": v(13.14, -9.52) * mm, "end": v(13.1, -10.02) * mm, "construction": true});
            skArc(sketch, "E17.24.11", {"start": v(12.77, -9.02) * mm, "mid": v(12.76, -8.54) * mm, "end": v(12.73, -8.06) * mm});
            skPoint(sketch, "E17.24.12", {"position": v(13.15, -9.02) * mm});
            skArc(sketch, "E17.24.13", {"start": v(13.4, -8.29) * mm, "mid": v(13.4, -8.14) * mm, "end": v(13.38, -8) * mm});
            skArc(sketch, "E17.24.14", {"start": v(13.53, -9.61) * mm, "mid": v(13.44, -9.66) * mm, "end": v(13.4, -9.75) * mm});
            skArc(sketch, "E17.24.15", {"start": v(13.53, -8.43) * mm, "mid": v(13.44, -8.38) * mm, "end": v(13.4, -8.29) * mm});
            skArc(sketch, "E17.25.0", {"start": v(13.53, -6.4) * mm, "mid": v(13.38, -6.38) * mm, "end": v(13.21, -6.37) * mm});
            skArc(sketch, "E17.25.1", {"start": v(13.94, -6.83) * mm, "mid": v(13.8, -6.56) * mm, "end": v(13.53, -6.4) * mm});
            skArc(sketch, "E17.25.2", {"start": v(12.58, -7.1) * mm, "mid": v(12.67, -7.58) * mm, "end": v(12.73, -8.06) * mm});
            skPoint(sketch, "E17.25.3", {"position": v(13.2, -6.98) * mm});
            skArc(sketch, "E17.25.4", {"start": v(13.73, -7.38) * mm, "mid": v(13.6, -7.47) * mm, "end": v(13.45, -7.53) * mm});
            skLineSegment(sketch, "E17.25.5", {"start": v(12.35, -6.17) * mm, "end": v(12.98, -5.98) * mm});
            skArc(sketch, "E17.25.6", {"start": v(13.34, -7.7) * mm, "mid": v(13.36, -7.84) * mm, "end": v(13.38, -8) * mm});
            skLineSegment(sketch, "E17.25.7", {"start": v(12.73, -8.06) * mm, "end": v(13.38, -8) * mm});
            skArc(sketch, "E17.25.8", {"start": v(13.94, -6.83) * mm, "mid": v(13.91, -7.14) * mm, "end": v(13.73, -7.38) * mm});
            skPoint(sketch, "E17.25.9", {"position": v(12.58, -7.1) * mm});
            skArc(sketch, "E17.25.10", {"start": v(12.95, -7.03) * mm, "mid": v(13.04, -7.52) * mm, "end": v(13.1, -8.02) * mm, "construction": true});
            skArc(sketch, "E17.25.11", {"start": v(12.58, -7.1) * mm, "mid": v(12.48, -6.63) * mm, "end": v(12.35, -6.17) * mm});
            skPoint(sketch, "E17.25.12", {"position": v(12.95, -7.03) * mm});
            skArc(sketch, "E17.25.13", {"start": v(13.06, -6.26) * mm, "mid": v(13.02, -6.12) * mm, "end": v(12.98, -5.98) * mm});
            skArc(sketch, "E17.25.14", {"start": v(13.45, -7.53) * mm, "mid": v(13.37, -7.6) * mm, "end": v(13.34, -7.7) * mm});
            skArc(sketch, "E17.25.15", {"start": v(13.21, -6.37) * mm, "mid": v(13.12, -6.35) * mm, "end": v(13.06, -6.26) * mm});
            skArc(sketch, "E17.26.0", {"start": v(12.82, -4.4) * mm, "mid": v(12.66, -4.4) * mm, "end": v(12.5, -4.42) * mm});
            skArc(sketch, "E17.26.1", {"start": v(13.3, -4.73) * mm, "mid": v(13.1, -4.5) * mm, "end": v(12.82, -4.4) * mm});
            skArc(sketch, "E17.26.2", {"start": v(12.03, -5.26) * mm, "mid": v(12.2, -5.7) * mm, "end": v(12.35, -6.17) * mm});
            skPoint(sketch, "E17.26.3", {"position": v(12.6, -5.02) * mm});
            skArc(sketch, "E17.26.4", {"start": v(13.2, -5.31) * mm, "mid": v(13.09, -5.42) * mm, "end": v(12.95, -5.52) * mm});
            skLineSegment(sketch, "E17.26.5", {"start": v(11.61, -4.39) * mm, "end": v(12.2, -4.08) * mm});
            skArc(sketch, "E17.26.6", {"start": v(12.89, -5.7) * mm, "mid": v(12.93, -5.83) * mm, "end": v(12.98, -5.98) * mm});
            skLineSegment(sketch, "E17.26.7", {"start": v(12.35, -6.17) * mm, "end": v(12.98, -5.98) * mm});
            skArc(sketch, "E17.26.8", {"start": v(13.3, -4.73) * mm, "mid": v(13.33, -5.04) * mm, "end": v(13.2, -5.31) * mm});
            skPoint(sketch, "E17.26.9", {"position": v(12.03, -5.26) * mm});
            skArc(sketch, "E17.26.10", {"start": v(12.37, -5.12) * mm, "mid": v(12.55, -5.58) * mm, "end": v(12.7, -6.06) * mm, "construction": true});
            skArc(sketch, "E17.26.11", {"start": v(12.03, -5.26) * mm, "mid": v(11.83, -4.82) * mm, "end": v(11.61, -4.39) * mm});
            skPoint(sketch, "E17.26.12", {"position": v(12.37, -5.12) * mm});
            skArc(sketch, "E17.26.13", {"start": v(12.33, -4.34) * mm, "mid": v(12.26, -4.21) * mm, "end": v(12.2, -4.08) * mm});
            skArc(sketch, "E17.26.14", {"start": v(12.95, -5.52) * mm, "mid": v(12.89, -5.6) * mm, "end": v(12.89, -5.7) * mm});
            skArc(sketch, "E17.26.15", {"start": v(12.5, -4.42) * mm, "mid": v(12.4, -4.41) * mm, "end": v(12.33, -4.34) * mm});
            skArc(sketch, "E17.27.0", {"start": v(11.73, -2.55) * mm, "mid": v(11.57, -2.59) * mm, "end": v(11.42, -2.65) * mm});
            skArc(sketch, "E17.27.1", {"start": v(12.26, -2.8) * mm, "mid": v(12.03, -2.6) * mm, "end": v(11.73, -2.55) * mm});
            skArc(sketch, "E17.27.2", {"start": v(11.12, -3.56) * mm, "mid": v(11.38, -3.97) * mm, "end": v(11.61, -4.39) * mm});
            skPoint(sketch, "E17.27.3", {"position": v(11.64, -3.21) * mm});
            skArc(sketch, "E17.27.4", {"start": v(12.28, -3.38) * mm, "mid": v(12.2, -3.52) * mm, "end": v(12.08, -3.63) * mm});
            skLineSegment(sketch, "E17.27.5", {"start": v(10.54, -2.79) * mm, "end": v(11.05, -2.37) * mm});
            skArc(sketch, "E17.27.6", {"start": v(12.05, -3.82) * mm, "mid": v(12.12, -3.95) * mm, "end": v(12.2, -4.08) * mm});
            skLineSegment(sketch, "E17.27.7", {"start": v(11.61, -4.39) * mm, "end": v(12.2, -4.08) * mm});
            skArc(sketch, "E17.27.8", {"start": v(12.26, -2.8) * mm, "mid": v(12.36, -3.09) * mm, "end": v(12.28, -3.38) * mm});
            skPoint(sketch, "E17.27.9", {"position": v(11.12, -3.56) * mm});
            skArc(sketch, "E17.27.10", {"start": v(11.43, -3.35) * mm, "mid": v(11.7, -3.78) * mm, "end": v(11.94, -4.21) * mm, "construction": true});
            skArc(sketch, "E17.27.11", {"start": v(11.12, -3.56) * mm, "mid": v(10.84, -3.17) * mm, "end": v(10.54, -2.79) * mm});
            skPoint(sketch, "E17.27.12", {"position": v(11.43, -3.35) * mm});
            skArc(sketch, "E17.27.13", {"start": v(11.24, -2.6) * mm, "mid": v(11.14, -2.49) * mm, "end": v(11.05, -2.37) * mm});
            skArc(sketch, "E17.27.14", {"start": v(12.08, -3.63) * mm, "mid": v(12.03, -3.72) * mm, "end": v(12.05, -3.82) * mm});
            skArc(sketch, "E17.27.15", {"start": v(11.42, -2.65) * mm, "mid": v(11.32, -2.66) * mm, "end": v(11.24, -2.6) * mm});
            skArc(sketch, "E17.28.0", {"start": v(10.3, -0.96) * mm, "mid": v(10.15, -1.03) * mm, "end": v(10.01, -1.12) * mm});
            skArc(sketch, "E17.28.1", {"start": v(10.87, -1.1) * mm, "mid": v(10.6, -0.95) * mm, "end": v(10.3, -0.96) * mm});
            skArc(sketch, "E17.28.2", {"start": v(9.9, -2.07) * mm, "mid": v(10.23, -2.42) * mm, "end": v(10.54, -2.79) * mm});
            skPoint(sketch, "E17.28.3", {"position": v(10.34, -1.63) * mm});
            skArc(sketch, "E17.28.4", {"start": v(11, -1.67) * mm, "mid": v(10.94, -1.82) * mm, "end": v(10.85, -1.95) * mm});
            skLineSegment(sketch, "E17.28.5", {"start": v(9.18, -1.43) * mm, "end": v(9.6, -0.92) * mm});
            skArc(sketch, "E17.28.6", {"start": v(10.86, -2.14) * mm, "mid": v(10.95, -2.26) * mm, "end": v(11.05, -2.37) * mm});
            skLineSegment(sketch, "E17.28.7", {"start": v(10.54, -2.79) * mm, "end": v(11.05, -2.37) * mm});
            skArc(sketch, "E17.28.8", {"start": v(10.87, -1.1) * mm, "mid": v(11.02, -1.36) * mm, "end": v(11, -1.67) * mm});
            skPoint(sketch, "E17.28.9", {"position": v(9.9, -2.07) * mm});
            skArc(sketch, "E17.28.10", {"start": v(10.16, -1.8) * mm, "mid": v(10.5, -2.17) * mm, "end": v(10.83, -2.55) * mm, "construction": true});
            skArc(sketch, "E17.28.11", {"start": v(9.9, -2.07) * mm, "mid": v(9.55, -1.74) * mm, "end": v(9.18, -1.43) * mm});
            skPoint(sketch, "E17.28.12", {"position": v(10.16, -1.8) * mm});
            skArc(sketch, "E17.28.13", {"start": v(9.82, -1.11) * mm, "mid": v(9.71, -1.01) * mm, "end": v(9.6, -0.92) * mm});
            skArc(sketch, "E17.28.14", {"start": v(10.85, -1.95) * mm, "mid": v(10.82, -2.05) * mm, "end": v(10.86, -2.14) * mm});
            skArc(sketch, "E17.28.15", {"start": v(10.01, -1.12) * mm, "mid": v(9.92, -1.15) * mm, "end": v(9.82, -1.11) * mm});
            skArc(sketch, "E17.29.0", {"start": v(8.59, 0.31) * mm, "mid": v(8.45, 0.22) * mm, "end": v(8.34, 0.1) * mm});
            skArc(sketch, "E17.29.1", {"start": v(9.17, 0.3) * mm, "mid": v(8.88, 0.39) * mm, "end": v(8.59, 0.31) * mm});
            skArc(sketch, "E17.29.2", {"start": v(8.4, -0.85) * mm, "mid": v(8.8, -1.13) * mm, "end": v(9.18, -1.43) * mm});
            skPoint(sketch, "E17.29.3", {"position": v(8.76, -0.33) * mm});
            skArc(sketch, "E17.29.4", {"start": v(9.42, -0.24) * mm, "mid": v(9.38, -0.4) * mm, "end": v(9.32, -0.55) * mm});
            skLineSegment(sketch, "E17.29.5", {"start": v(7.58, -0.36) * mm, "end": v(7.89, 0.22) * mm});
            skArc(sketch, "E17.29.6", {"start": v(9.36, -0.73) * mm, "mid": v(9.48, -0.82) * mm, "end": v(9.6, -0.92) * mm});
            skLineSegment(sketch, "E17.29.7", {"start": v(9.18, -1.43) * mm, "end": v(9.6, -0.92) * mm});
            skArc(sketch, "E17.29.8", {"start": v(9.17, 0.3) * mm, "mid": v(9.37, 0.06) * mm, "end": v(9.42, -0.24) * mm});
            skPoint(sketch, "E17.29.9", {"position": v(8.4, -0.85) * mm});
            skArc(sketch, "E17.29.10", {"start": v(8.62, -0.54) * mm, "mid": v(9.03, -0.83) * mm, "end": v(9.42, -1.13) * mm, "construction": true});
            skArc(sketch, "E17.29.11", {"start": v(8.4, -0.85) * mm, "mid": v(8, -0.6) * mm, "end": v(7.58, -0.36) * mm});
            skPoint(sketch, "E17.29.12", {"position": v(8.62, -0.54) * mm});
            skArc(sketch, "E17.29.13", {"start": v(8.15, 0.08) * mm, "mid": v(8.02, 0.15) * mm, "end": v(7.89, 0.22) * mm});
            skArc(sketch, "E17.29.14", {"start": v(9.32, -0.55) * mm, "mid": v(9.3, -0.65) * mm, "end": v(9.36, -0.73) * mm});
            skArc(sketch, "E17.29.15", {"start": v(8.34, 0.1) * mm, "mid": v(8.25, 0.06) * mm, "end": v(8.15, 0.08) * mm});
            skArc(sketch, "E17.30.0", {"start": v(6.66, 1.23) * mm, "mid": v(6.54, 1.12) * mm, "end": v(6.45, 0.99) * mm});
            skArc(sketch, "E17.30.1", {"start": v(7.24, 1.33) * mm, "mid": v(6.93, 1.37) * mm, "end": v(6.66, 1.23) * mm});
            skArc(sketch, "E17.30.2", {"start": v(6.7, 0.06) * mm, "mid": v(7.15, -0.14) * mm, "end": v(7.58, -0.36) * mm});
            skPoint(sketch, "E17.30.3", {"position": v(6.95, 0.64) * mm});
            skArc(sketch, "E17.30.4", {"start": v(7.58, 0.85) * mm, "mid": v(7.57, 0.7) * mm, "end": v(7.55, 0.53) * mm});
            skLineSegment(sketch, "E17.30.5", {"start": v(5.8, 0.38) * mm, "end": v(6, 1) * mm});
            skArc(sketch, "E17.30.6", {"start": v(7.62, 0.36) * mm, "mid": v(7.76, 0.3) * mm, "end": v(7.89, 0.22) * mm});
            skLineSegment(sketch, "E17.30.7", {"start": v(7.58, -0.36) * mm, "end": v(7.89, 0.22) * mm});
            skArc(sketch, "E17.30.8", {"start": v(7.24, 1.33) * mm, "mid": v(7.48, 1.14) * mm, "end": v(7.58, 0.85) * mm});
            skPoint(sketch, "E17.30.9", {"position": v(6.7, 0.06) * mm});
            skArc(sketch, "E17.30.10", {"start": v(6.85, 0.4) * mm, "mid": v(7.31, 0.2) * mm, "end": v(7.76, -0.02) * mm, "construction": true});
            skArc(sketch, "E17.30.11", {"start": v(6.7, 0.06) * mm, "mid": v(6.26, 0.23) * mm, "end": v(5.8, 0.38) * mm});
            skPoint(sketch, "E17.30.12", {"position": v(6.85, 0.4) * mm});
            skArc(sketch, "E17.30.13", {"start": v(6.28, 0.92) * mm, "mid": v(6.13, 0.96) * mm, "end": v(6, 1) * mm});
            skArc(sketch, "E17.30.14", {"start": v(7.55, 0.53) * mm, "mid": v(7.55, 0.43) * mm, "end": v(7.62, 0.36) * mm});
            skArc(sketch, "E17.30.15", {"start": v(6.45, 0.99) * mm, "mid": v(6.38, 0.92) * mm, "end": v(6.28, 0.92) * mm});
            skArc(sketch, "E17.31.0", {"start": v(4.58, 1.76) * mm, "mid": v(4.5, 1.62) * mm, "end": v(4.43, 1.48) * mm});
            skArc(sketch, "E17.31.1", {"start": v(5.13, 1.97) * mm, "mid": v(4.83, 1.94) * mm, "end": v(4.58, 1.76) * mm});
            skArc(sketch, "E17.31.2", {"start": v(4.87, 0.62) * mm, "mid": v(5.34, 0.51) * mm, "end": v(5.8, 0.38) * mm});
            skPoint(sketch, "E17.31.3", {"position": v(4.99, 1.23) * mm});
            skArc(sketch, "E17.31.4", {"start": v(5.56, 1.57) * mm, "mid": v(5.6, 1.4) * mm, "end": v(5.6, 1.25) * mm});
            skArc(sketch, "E17.31.6", {"start": v(5.7, 1.1) * mm, "mid": v(5.85, 1.05) * mm, "end": v(6, 1) * mm});
            skLineSegment(sketch, "E17.31.7", {"start": v(5.8, 0.38) * mm, "end": v(6, 1) * mm});
            skArc(sketch, "E17.31.8", {"start": v(5.13, 1.97) * mm, "mid": v(5.4, 1.83) * mm, "end": v(5.56, 1.57) * mm});
            skPoint(sketch, "E17.31.9", {"position": v(4.87, 0.62) * mm});
            skArc(sketch, "E17.31.10", {"start": v(4.94, 0.98) * mm, "mid": v(5.43, 0.87) * mm, "end": v(5.91, 0.74) * mm, "construction": true});
            skArc(sketch, "E17.31.11", {"start": v(4.87, 0.62) * mm, "mid": v(4.4, 0.7) * mm, "end": v(3.91, 0.76) * mm});
            skPoint(sketch, "E17.31.12", {"position": v(4.94, 0.98) * mm});
            skArc(sketch, "E17.31.13", {"start": v(4.27, 1.38) * mm, "mid": v(4.12, 1.4) * mm, "end": v(3.98, 1.4) * mm});
            skArc(sketch, "E17.31.14", {"start": v(5.6, 1.25) * mm, "mid": v(5.62, 1.15) * mm, "end": v(5.7, 1.1) * mm});
            skArc(sketch, "E17.31.15", {"start": v(4.43, 1.48) * mm, "mid": v(4.37, 1.4) * mm, "end": v(4.27, 1.38) * mm});
            skSolve(sketch);
        }
        {
            var Q0;
            Q0=qSketchRegion(id+"F0",true);
            extrude(context, id + "F1", {"entities" : qUnion([Q0]), "depth" : 6 * mm});
        }
    });
